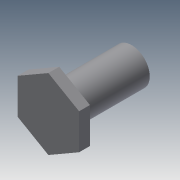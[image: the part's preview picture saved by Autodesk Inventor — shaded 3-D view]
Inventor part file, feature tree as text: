
AUTODESK INVENTOR PART (.ipt)
format: ipt  version: 2015 (Build 190159000, 159)  size: 84,992 bytes
history: native  units: mm
features: extrude x2, sketch x2
ambient origin geometry x8: Origin, YZ Plane, XZ Plane, XY Plane, X Axis, Y Axis, Z Axis, Center Point
bodies: Solid1 (feature_tree)
feature tree (4):
  extrude  "Extrusion1"  Depth=3.0mm
  extrude  "Extrusion2"  Depth=20.0mm TaperAngle=0.0deg
  sketch  "Sketch1"  dims[d1=3.0mm d2=0.0mm d3=19.6mm]
  sketch  "Sketch2"  dims[d4=10.0mm d5=20.0mm d6=0.0mm]
